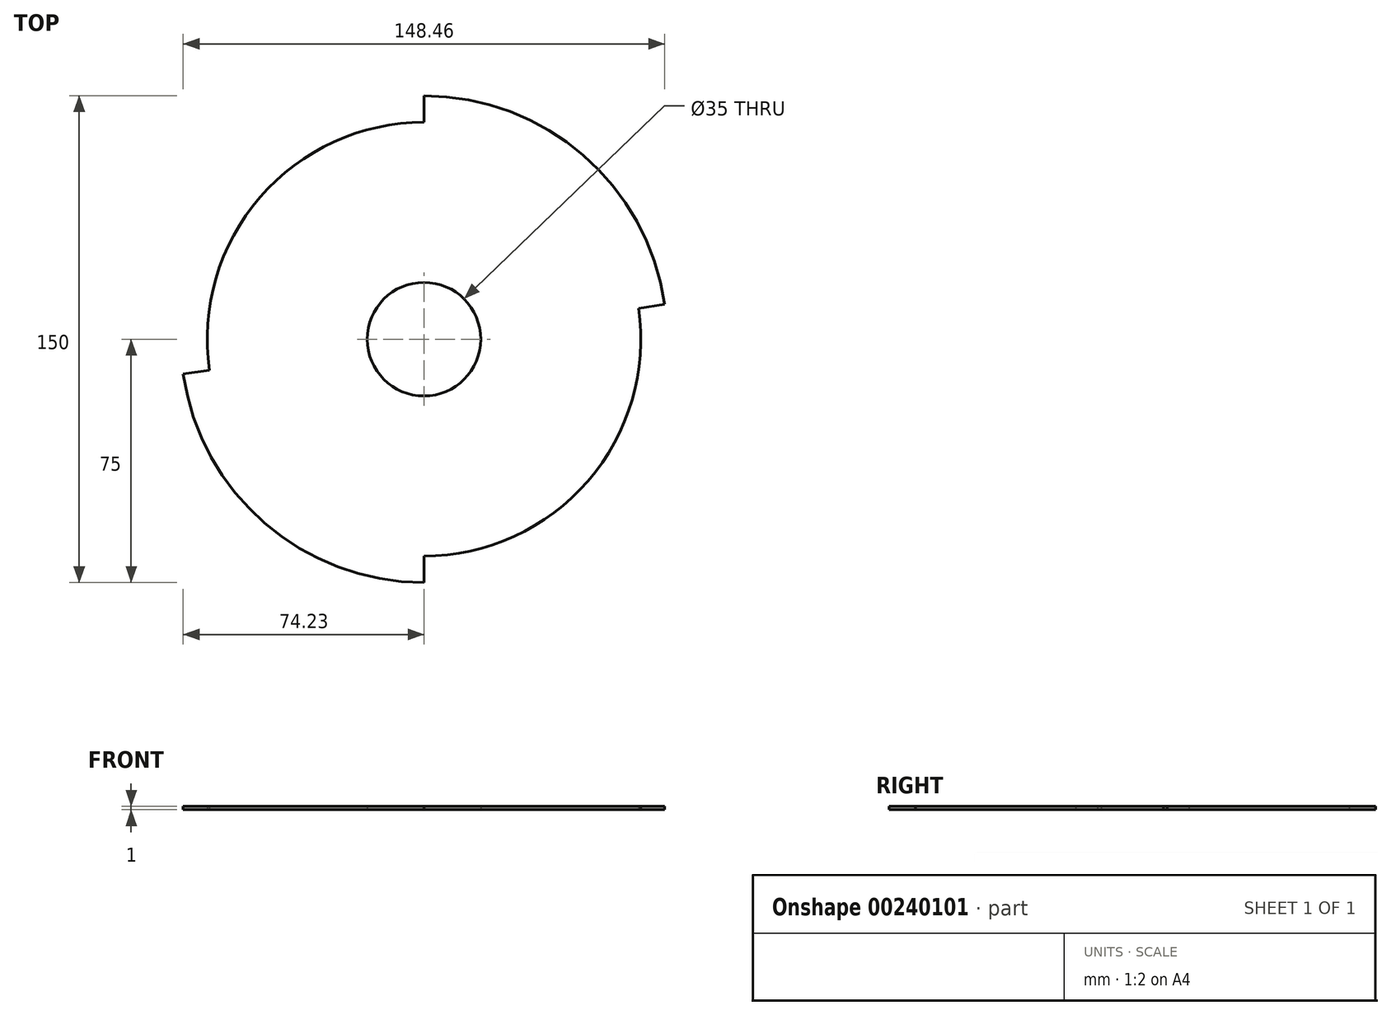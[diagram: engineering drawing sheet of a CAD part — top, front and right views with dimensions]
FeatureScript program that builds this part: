
annotation { "Feature Type Name" : "Feature", "Feature Type Description" : "" }
export const myFeature = defineFeature(function(context is Context, id is Id, definition is map)
    precondition{}
    {
        {
            var Q0;
            Q0=qCreatedBy(makeId("Top.planeOp"),FACE);
            var sketch = newSketch(context, id + "F0", { "sketchPlane" : qUnion([Q0])});
            skCircle(sketch, "E0", {"center": v(0, 0) * mm, "radius": 75 * mm});
            skCircle(sketch, "E1", {"center": v(0, 0) * mm, "radius": 17.5 * mm});
            skCircle(sketch, "E2", {"center": v(0, 0) * mm, "radius": 66.83 * mm});
            skPoint(sketch, "E3", {"position": v(66.15, 9.54) * mm});
            skLineSegment(sketch, "E4", {"start": v(66.15, 9.54) * mm, "end": v(74.23, 10.7) * mm});
            skLineSegment(sketch, "E5.1.0", {"start": v(-66.15, -9.54) * mm, "end": v(-74.23, -10.7) * mm});
            skLineSegment(sketch, "E6", {"start": v(0, 75) * mm, "end": v(0, 66.83) * mm});
            skLineSegment(sketch, "E7.1.0", {"start": v(0, -75) * mm, "end": v(0, -66.83) * mm});
            skSolve(sketch);
        }
        {
            var Q0;
            {var subQ0=sQuery(id+"F0.wireOp",EDGE,"E5.1.0");Q0=makeQuery(id+"F0.imprint","IMPRINT",FACE,{"disambiguationData":[TD([[makeQuery(id+"F0.imprint","IMPRINT",EDGE,{"derivedFrom":subQ0}),1.0]])]});}
            var Q1;
            {var subQ0=sQuery(id+"F0.wireOp",EDGE,"E4");Q1=makeQuery(id+"F0.imprint","IMPRINT",FACE,{"disambiguationData":[TD([[makeQuery(id+"F0.imprint","IMPRINT",EDGE,{"derivedFrom":subQ0}),1.0]])]});}
            var Q2;
            Q2=makeQuery(id+"F0.imprint","IMPRINT",FACE,{"disambiguationData":[TD([[makeQuery(id+"F0.imprint","IMPRINT",EDGE,{"derivedFrom":sQuery(id+"F0.wireOp",EDGE,"E1")}),-1.0]])]});
            extrude(context, id + "F1", {"entities" : qUnion([Q0, Q1, Q2]), "depth" : 1 * mm, "offsetDistance" : 25 * mm});
        }
    });
